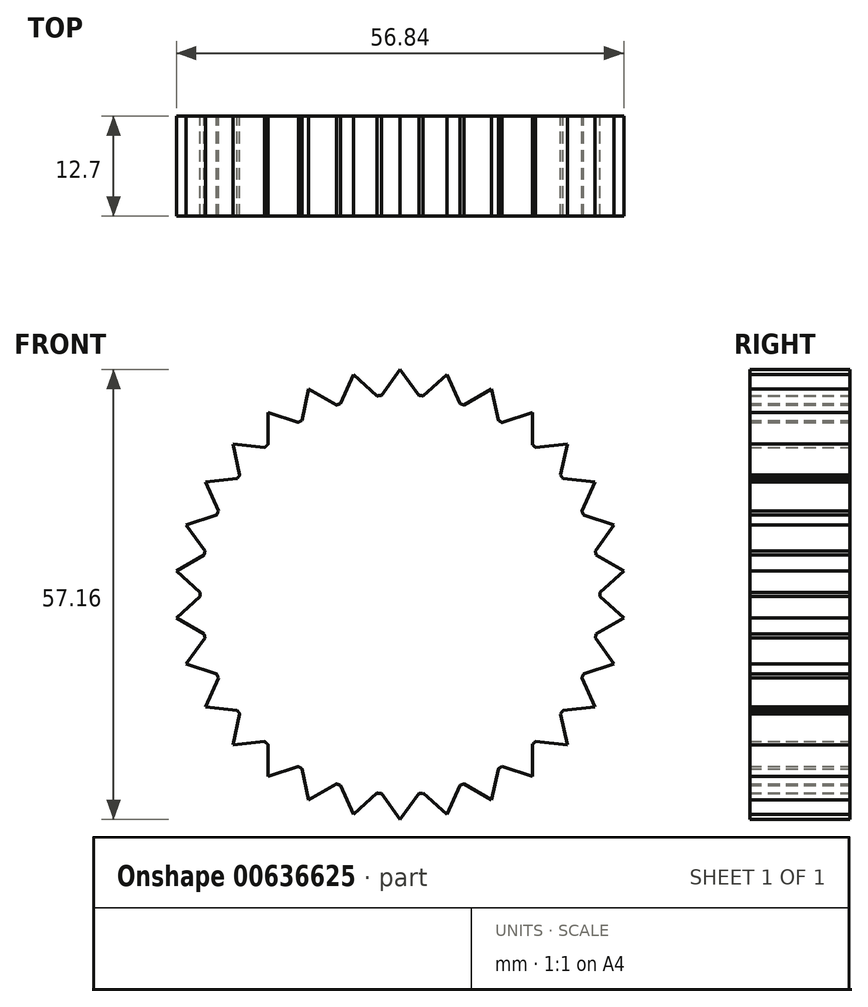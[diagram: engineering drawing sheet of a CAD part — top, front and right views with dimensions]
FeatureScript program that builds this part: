
annotation { "Feature Type Name" : "Feature", "Feature Type Description" : "" }
export const myFeature = defineFeature(function(context is Context, id is Id, definition is map)
    precondition{}
    {
        {
            var Q0;
            Q0=qCreatedBy(makeId("Front.planeOp"),FACE);
            var sketch = newSketch(context, id + "F0", { "sketchPlane" : qUnion([Q0])});
            skCircle(sketch, "E0", {"center": v(0, 0) * mm, "radius": 25.4 * mm});
            skLineSegment(sketch, "E1", {"start": v(0, 25.4) * mm, "end": v(0, 28.58) * mm, "construction": true});
            skLineSegment(sketch, "E2", {"start": v(0, 28.58) * mm, "end": v(-2.38, 25.29) * mm});
            skLineSegment(sketch, "E3.MirrorCS", {"start": v(0, 28.58) * mm, "end": v(2.38, 25.29) * mm});
            skLineSegment(sketch, "E4.2.0", {"start": v(-24.75, -14.29) * mm, "end": v(-23.1, -10.58) * mm});
            skLineSegment(sketch, "E5.2.3.0", {"start": v(0, -28.58) * mm, "end": v(-2.38, -25.29) * mm});
            skLineSegment(sketch, "E5.2.4.0", {"start": v(24.75, -14.29) * mm, "end": v(20.7, -14.7) * mm});
            skLineSegment(sketch, "E6.1.0", {"start": v(-5.94, 27.95) * mm, "end": v(-7.59, 24.24) * mm});
            skLineSegment(sketch, "E6.1.1", {"start": v(-5.94, 27.95) * mm, "end": v(-2.93, 25.23) * mm});
            skLineSegment(sketch, "E6.2.0", {"start": v(-11.62, 26.1) * mm, "end": v(-12.46, 22.13) * mm});
            skLineSegment(sketch, "E6.2.1", {"start": v(-11.62, 26.1) * mm, "end": v(-8.1, 24.07) * mm});
            skLineSegment(sketch, "E7.2.3.0", {"start": v(-16.8, 23.12) * mm, "end": v(-16.8, 19.06) * mm});
            skLineSegment(sketch, "E7.3.3.0", {"start": v(-16.8, 23.12) * mm, "end": v(-12.94, 21.86) * mm});
            skLineSegment(sketch, "E7.2.4.0", {"start": v(-21.24, 19.12) * mm, "end": v(-20.39, 15.15) * mm});
            skLineSegment(sketch, "E7.3.4.0", {"start": v(-21.24, 19.12) * mm, "end": v(-17.2, 18.7) * mm});
            skLineSegment(sketch, "E7.2.5.0", {"start": v(-24.75, 14.29) * mm, "end": v(-23.1, 10.58) * mm});
            skLineSegment(sketch, "E7.3.5.0", {"start": v(-24.75, 14.29) * mm, "end": v(-20.7, 14.7) * mm});
            skLineSegment(sketch, "E8.2.6.0", {"start": v(-27.18, 8.83) * mm, "end": v(-24.79, 5.55) * mm});
            skLineSegment(sketch, "E8.3.6.0", {"start": v(-27.18, 8.83) * mm, "end": v(-23.31, 10.08) * mm});
            skLineSegment(sketch, "E8.2.7.0", {"start": v(-28.42, 2.99) * mm, "end": v(-25.4, 0.27) * mm});
            skLineSegment(sketch, "E8.3.7.0", {"start": v(-28.42, 2.99) * mm, "end": v(-24.9, 5.01) * mm});
            skLineSegment(sketch, "E8.2.8.0", {"start": v(-28.42, -2.99) * mm, "end": v(-24.9, -5.01) * mm});
            skLineSegment(sketch, "E8.3.8.0", {"start": v(-28.42, -2.99) * mm, "end": v(-25.4, -0.27) * mm});
            skLineSegment(sketch, "E8.2.9.0", {"start": v(-27.18, -8.83) * mm, "end": v(-23.31, -10.08) * mm});
            skLineSegment(sketch, "E8.3.9.0", {"start": v(-27.18, -8.83) * mm, "end": v(-24.79, -5.55) * mm});
            skLineSegment(sketch, "E8.2.10.0", {"start": v(-24.75, -14.29) * mm, "end": v(-20.7, -14.7) * mm});
            skLineSegment(sketch, "E8.2.11.0", {"start": v(-21.24, -19.12) * mm, "end": v(-17.2, -18.7) * mm});
            skLineSegment(sketch, "E8.3.11.0", {"start": v(-21.24, -19.12) * mm, "end": v(-20.39, -15.15) * mm});
            skLineSegment(sketch, "E8.2.12.0", {"start": v(-16.8, -23.12) * mm, "end": v(-12.94, -21.86) * mm});
            skLineSegment(sketch, "E8.3.12.0", {"start": v(-16.8, -23.12) * mm, "end": v(-16.8, -19.06) * mm});
            skLineSegment(sketch, "E8.2.13.0", {"start": v(-11.62, -26.1) * mm, "end": v(-8.1, -24.07) * mm});
            skLineSegment(sketch, "E8.3.13.0", {"start": v(-11.62, -26.1) * mm, "end": v(-12.46, -22.13) * mm});
            skLineSegment(sketch, "E8.2.14.0", {"start": v(-5.94, -27.95) * mm, "end": v(-2.93, -25.23) * mm});
            skLineSegment(sketch, "E8.3.14.0", {"start": v(-5.94, -27.95) * mm, "end": v(-7.59, -24.24) * mm});
            skLineSegment(sketch, "E8.2.15.0", {"start": v(0, -28.58) * mm, "end": v(2.38, -25.29) * mm});
            skLineSegment(sketch, "E8.2.16.0", {"start": v(5.94, -27.95) * mm, "end": v(7.59, -24.24) * mm});
            skLineSegment(sketch, "E8.3.16.0", {"start": v(5.94, -27.95) * mm, "end": v(2.93, -25.23) * mm});
            skLineSegment(sketch, "E8.2.17.0", {"start": v(11.62, -26.1) * mm, "end": v(12.46, -22.13) * mm});
            skLineSegment(sketch, "E8.3.17.0", {"start": v(11.62, -26.1) * mm, "end": v(8.1, -24.07) * mm});
            skLineSegment(sketch, "E8.2.18.0", {"start": v(16.8, -23.12) * mm, "end": v(16.8, -19.06) * mm});
            skLineSegment(sketch, "E8.3.18.0", {"start": v(16.8, -23.12) * mm, "end": v(12.94, -21.86) * mm});
            skLineSegment(sketch, "E8.2.19.0", {"start": v(21.24, -19.12) * mm, "end": v(20.39, -15.15) * mm});
            skLineSegment(sketch, "E8.3.19.0", {"start": v(21.24, -19.12) * mm, "end": v(17.2, -18.7) * mm});
            skLineSegment(sketch, "E8.2.20.0", {"start": v(24.75, -14.29) * mm, "end": v(23.1, -10.58) * mm});
            skLineSegment(sketch, "E8.2.21.0", {"start": v(27.18, -8.83) * mm, "end": v(24.79, -5.55) * mm});
            skLineSegment(sketch, "E8.3.21.0", {"start": v(27.18, -8.83) * mm, "end": v(23.31, -10.08) * mm});
            skLineSegment(sketch, "E8.2.22.0", {"start": v(28.42, -2.99) * mm, "end": v(25.4, -0.27) * mm});
            skLineSegment(sketch, "E8.3.22.0", {"start": v(28.42, -2.99) * mm, "end": v(24.9, -5.01) * mm});
            skLineSegment(sketch, "E8.2.23.0", {"start": v(28.42, 2.99) * mm, "end": v(24.9, 5.01) * mm});
            skLineSegment(sketch, "E8.3.23.0", {"start": v(28.42, 2.99) * mm, "end": v(25.4, 0.27) * mm});
            skLineSegment(sketch, "E8.2.24.0", {"start": v(27.18, 8.83) * mm, "end": v(23.31, 10.08) * mm});
            skLineSegment(sketch, "E8.3.24.0", {"start": v(27.18, 8.83) * mm, "end": v(24.79, 5.55) * mm});
            skLineSegment(sketch, "E8.2.25.0", {"start": v(24.75, 14.29) * mm, "end": v(20.7, 14.7) * mm});
            skLineSegment(sketch, "E8.3.25.0", {"start": v(24.75, 14.29) * mm, "end": v(23.1, 10.58) * mm});
            skLineSegment(sketch, "E8.2.26.0", {"start": v(21.24, 19.12) * mm, "end": v(17.2, 18.7) * mm});
            skLineSegment(sketch, "E8.3.26.0", {"start": v(21.24, 19.12) * mm, "end": v(20.39, 15.15) * mm});
            skLineSegment(sketch, "E8.2.27.0", {"start": v(16.8, 23.12) * mm, "end": v(12.94, 21.86) * mm});
            skLineSegment(sketch, "E8.3.27.0", {"start": v(16.8, 23.12) * mm, "end": v(16.8, 19.06) * mm});
            skLineSegment(sketch, "E8.2.28.0", {"start": v(11.62, 26.1) * mm, "end": v(8.1, 24.07) * mm});
            skLineSegment(sketch, "E8.3.28.0", {"start": v(11.62, 26.1) * mm, "end": v(12.46, 22.13) * mm});
            skLineSegment(sketch, "E8.2.29.0", {"start": v(5.94, 27.95) * mm, "end": v(2.93, 25.23) * mm});
            skLineSegment(sketch, "E8.3.29.0", {"start": v(5.94, 27.95) * mm, "end": v(7.59, 24.24) * mm});
            skSolve(sketch);
        }
        {
            var Q0;
            {var subQ0=sQuery(id+"F0.wireOp",EDGE,"E0");var subQ33=makeQuery(id+"F0.imprint","INTERSECT",VERTEX,{"derivedFrom":[sQuery(id+"F0.wireOp",EDGE,"E8.2.22.0"),subQ0]});Q0=makeQuery(id+"F0.imprint","IMPRINT",FACE,{"disambiguationData":[TD([[makeQuery(id+"F0.imprint","IMPRINT",EDGE,{"disambiguationData":[TD([[subQ33,1.0]])],"derivedFrom":subQ0}),1.0]])]});}
            var Q1;
            {var subQ0=sQuery(id+"F0.wireOp",EDGE,"E7.2.5.0");Q1=makeQuery(id+"F0.imprint","IMPRINT",FACE,{"disambiguationData":[TD([[makeQuery(id+"F0.imprint","IMPRINT",EDGE,{"derivedFrom":subQ0}),1.0]])]});}
            var Q2;
            {var subQ0=sQuery(id+"F0.wireOp",EDGE,"E7.2.4.0");Q2=makeQuery(id+"F0.imprint","IMPRINT",FACE,{"disambiguationData":[TD([[makeQuery(id+"F0.imprint","IMPRINT",EDGE,{"derivedFrom":subQ0}),1.0]])]});}
            var Q3;
            {var subQ0=sQuery(id+"F0.wireOp",EDGE,"E7.2.3.0");Q3=makeQuery(id+"F0.imprint","IMPRINT",FACE,{"disambiguationData":[TD([[makeQuery(id+"F0.imprint","IMPRINT",EDGE,{"derivedFrom":subQ0}),1.0]])]});}
            var Q4;
            {var subQ0=sQuery(id+"F0.wireOp",EDGE,"E6.2.0");Q4=makeQuery(id+"F0.imprint","IMPRINT",FACE,{"disambiguationData":[TD([[makeQuery(id+"F0.imprint","IMPRINT",EDGE,{"derivedFrom":subQ0}),1.0]])]});}
            var Q5;
            {var subQ0=sQuery(id+"F0.wireOp",EDGE,"E6.1.0");Q5=makeQuery(id+"F0.imprint","IMPRINT",FACE,{"disambiguationData":[TD([[makeQuery(id+"F0.imprint","IMPRINT",EDGE,{"derivedFrom":subQ0}),1.0]])]});}
            var Q6;
            {var subQ0=sQuery(id+"F0.wireOp",EDGE,"E2");Q6=makeQuery(id+"F0.imprint","IMPRINT",FACE,{"disambiguationData":[TD([[makeQuery(id+"F0.imprint","IMPRINT",EDGE,{"derivedFrom":subQ0}),1.0]])]});}
            var Q7;
            {var subQ0=sQuery(id+"F0.wireOp",EDGE,"E8.2.29.0");Q7=makeQuery(id+"F0.imprint","IMPRINT",FACE,{"disambiguationData":[TD([[makeQuery(id+"F0.imprint","IMPRINT",EDGE,{"derivedFrom":subQ0}),1.0]])]});}
            var Q8;
            {var subQ0=sQuery(id+"F0.wireOp",EDGE,"E8.2.28.0");Q8=makeQuery(id+"F0.imprint","IMPRINT",FACE,{"disambiguationData":[TD([[makeQuery(id+"F0.imprint","IMPRINT",EDGE,{"derivedFrom":subQ0}),1.0]])]});}
            var Q9;
            {var subQ0=sQuery(id+"F0.wireOp",EDGE,"E8.2.27.0");Q9=makeQuery(id+"F0.imprint","IMPRINT",FACE,{"disambiguationData":[TD([[makeQuery(id+"F0.imprint","IMPRINT",EDGE,{"derivedFrom":subQ0}),1.0]])]});}
            var Q10;
            {var subQ0=sQuery(id+"F0.wireOp",EDGE,"E8.2.26.0");Q10=makeQuery(id+"F0.imprint","IMPRINT",FACE,{"disambiguationData":[TD([[makeQuery(id+"F0.imprint","IMPRINT",EDGE,{"derivedFrom":subQ0}),1.0]])]});}
            var Q11;
            {var subQ0=sQuery(id+"F0.wireOp",EDGE,"E8.2.25.0");Q11=makeQuery(id+"F0.imprint","IMPRINT",FACE,{"disambiguationData":[TD([[makeQuery(id+"F0.imprint","IMPRINT",EDGE,{"derivedFrom":subQ0}),1.0]])]});}
            var Q12;
            {var subQ0=sQuery(id+"F0.wireOp",EDGE,"E8.2.24.0");Q12=makeQuery(id+"F0.imprint","IMPRINT",FACE,{"disambiguationData":[TD([[makeQuery(id+"F0.imprint","IMPRINT",EDGE,{"derivedFrom":subQ0}),1.0]])]});}
            var Q13;
            {var subQ0=sQuery(id+"F0.wireOp",EDGE,"E8.2.23.0");Q13=makeQuery(id+"F0.imprint","IMPRINT",FACE,{"disambiguationData":[TD([[makeQuery(id+"F0.imprint","IMPRINT",EDGE,{"derivedFrom":subQ0}),1.0]])]});}
            var Q14;
            {var subQ0=sQuery(id+"F0.wireOp",EDGE,"E8.2.22.0");Q14=makeQuery(id+"F0.imprint","IMPRINT",FACE,{"disambiguationData":[TD([[makeQuery(id+"F0.imprint","IMPRINT",EDGE,{"derivedFrom":subQ0}),1.0]])]});}
            var Q15;
            {var subQ0=sQuery(id+"F0.wireOp",EDGE,"E8.2.21.0");Q15=makeQuery(id+"F0.imprint","IMPRINT",FACE,{"disambiguationData":[TD([[makeQuery(id+"F0.imprint","IMPRINT",EDGE,{"derivedFrom":subQ0}),1.0]])]});}
            var Q16;
            {var subQ0=sQuery(id+"F0.wireOp",EDGE,"E8.2.20.0");Q16=makeQuery(id+"F0.imprint","IMPRINT",FACE,{"disambiguationData":[TD([[makeQuery(id+"F0.imprint","IMPRINT",EDGE,{"derivedFrom":subQ0}),1.0]])]});}
            var Q17;
            {var subQ0=sQuery(id+"F0.wireOp",EDGE,"E8.2.19.0");Q17=makeQuery(id+"F0.imprint","IMPRINT",FACE,{"disambiguationData":[TD([[makeQuery(id+"F0.imprint","IMPRINT",EDGE,{"derivedFrom":subQ0}),1.0]])]});}
            var Q18;
            {var subQ0=sQuery(id+"F0.wireOp",EDGE,"E8.2.18.0");Q18=makeQuery(id+"F0.imprint","IMPRINT",FACE,{"disambiguationData":[TD([[makeQuery(id+"F0.imprint","IMPRINT",EDGE,{"derivedFrom":subQ0}),1.0]])]});}
            var Q19;
            {var subQ0=sQuery(id+"F0.wireOp",EDGE,"E8.2.17.0");Q19=makeQuery(id+"F0.imprint","IMPRINT",FACE,{"disambiguationData":[TD([[makeQuery(id+"F0.imprint","IMPRINT",EDGE,{"derivedFrom":subQ0}),1.0]])]});}
            var Q20;
            {var subQ0=sQuery(id+"F0.wireOp",EDGE,"E8.2.16.0");Q20=makeQuery(id+"F0.imprint","IMPRINT",FACE,{"disambiguationData":[TD([[makeQuery(id+"F0.imprint","IMPRINT",EDGE,{"derivedFrom":subQ0}),1.0]])]});}
            var Q21;
            {var subQ0=sQuery(id+"F0.wireOp",EDGE,"E8.2.15.0");Q21=makeQuery(id+"F0.imprint","IMPRINT",FACE,{"disambiguationData":[TD([[makeQuery(id+"F0.imprint","IMPRINT",EDGE,{"derivedFrom":subQ0}),1.0]])]});}
            var Q22;
            {var subQ0=sQuery(id+"F0.wireOp",EDGE,"E8.2.14.0");Q22=makeQuery(id+"F0.imprint","IMPRINT",FACE,{"disambiguationData":[TD([[makeQuery(id+"F0.imprint","IMPRINT",EDGE,{"derivedFrom":subQ0}),1.0]])]});}
            var Q23;
            {var subQ0=sQuery(id+"F0.wireOp",EDGE,"E8.2.13.0");Q23=makeQuery(id+"F0.imprint","IMPRINT",FACE,{"disambiguationData":[TD([[makeQuery(id+"F0.imprint","IMPRINT",EDGE,{"derivedFrom":subQ0}),1.0]])]});}
            var Q24;
            {var subQ0=sQuery(id+"F0.wireOp",EDGE,"E8.2.12.0");Q24=makeQuery(id+"F0.imprint","IMPRINT",FACE,{"disambiguationData":[TD([[makeQuery(id+"F0.imprint","IMPRINT",EDGE,{"derivedFrom":subQ0}),1.0]])]});}
            var Q25;
            {var subQ0=sQuery(id+"F0.wireOp",EDGE,"E8.2.11.0");Q25=makeQuery(id+"F0.imprint","IMPRINT",FACE,{"disambiguationData":[TD([[makeQuery(id+"F0.imprint","IMPRINT",EDGE,{"derivedFrom":subQ0}),1.0]])]});}
            var Q26;
            {var subQ0=sQuery(id+"F0.wireOp",EDGE,"E8.2.10.0");Q26=makeQuery(id+"F0.imprint","IMPRINT",FACE,{"disambiguationData":[TD([[makeQuery(id+"F0.imprint","IMPRINT",EDGE,{"derivedFrom":subQ0}),1.0]])]});}
            var Q27;
            {var subQ0=sQuery(id+"F0.wireOp",EDGE,"E8.2.9.0");Q27=makeQuery(id+"F0.imprint","IMPRINT",FACE,{"disambiguationData":[TD([[makeQuery(id+"F0.imprint","IMPRINT",EDGE,{"derivedFrom":subQ0}),1.0]])]});}
            var Q28;
            {var subQ0=sQuery(id+"F0.wireOp",EDGE,"E8.2.8.0");Q28=makeQuery(id+"F0.imprint","IMPRINT",FACE,{"disambiguationData":[TD([[makeQuery(id+"F0.imprint","IMPRINT",EDGE,{"derivedFrom":subQ0}),1.0]])]});}
            var Q29;
            {var subQ0=sQuery(id+"F0.wireOp",EDGE,"E8.2.7.0");Q29=makeQuery(id+"F0.imprint","IMPRINT",FACE,{"disambiguationData":[TD([[makeQuery(id+"F0.imprint","IMPRINT",EDGE,{"derivedFrom":subQ0}),1.0]])]});}
            var Q30;
            {var subQ0=sQuery(id+"F0.wireOp",EDGE,"E8.2.6.0");Q30=makeQuery(id+"F0.imprint","IMPRINT",FACE,{"disambiguationData":[TD([[makeQuery(id+"F0.imprint","IMPRINT",EDGE,{"derivedFrom":subQ0}),1.0]])]});}
            extrude(context, id + "F1", {"entities" : qUnion([Q0, Q1, Q2, Q3, Q4, Q5, Q6, Q7, Q8, Q9, Q10, Q11, Q12, Q13, Q14, Q15, Q16, Q17, Q18, Q19, Q20, Q21, Q22, Q23, Q24, Q25, Q26, Q27, Q28, Q29, Q30]), "depth" : 12.7 * mm, "offsetDistance" : 25.4 * mm});
        }
    });
